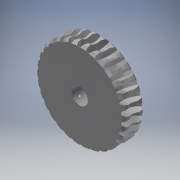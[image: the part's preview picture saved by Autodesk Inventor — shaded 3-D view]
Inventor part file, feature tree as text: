
AUTODESK INVENTOR PART (.ipt)
format: ipt  version: 2018 (Build 220112000, 112)  size: 883,712 bytes
history: native  units: in
note: dims shown in document units (in); Inventor stores cm internally (conversion verified against a paired STEP export)
features: other x3, sketch x2, hole x1
ambient origin geometry x8: Origin, YZ Plane, XZ Plane, XY Plane, X Axis, Y Axis, Z Axis, Center Point
bodies: Solid1 (feature_tree)
feature tree (6):
  other  "Worm Gear"
  hole  "Hole1"  [1 undecoded]
  sketch  "Sketch2"  dims[d2=0.5in d3=0.75in d4=0.375in d5=0.25in d6=0.5635in d7=1.0in d8=0.8108in]
  other  "Solid1::Worm Gear"
  other  "TaggingFeature1"
  sketch  "Sketch1"  dims[d0=0.315in d1=0.5in]
note: 1 required parameter value undecoded (feature->parameter linkage not recoverable at this tier; creation-order binding heuristic only, values carry confidence <= 0.55)
